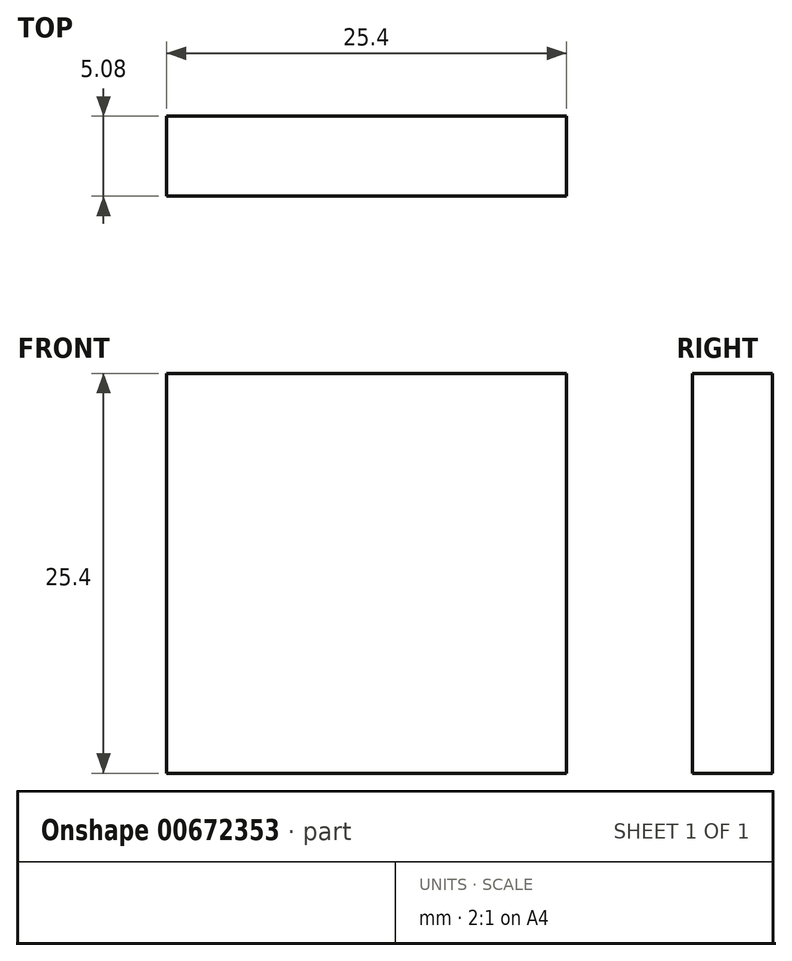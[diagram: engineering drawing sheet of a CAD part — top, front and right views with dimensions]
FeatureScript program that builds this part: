
annotation { "Feature Type Name" : "Feature", "Feature Type Description" : "" }
export const myFeature = defineFeature(function(context is Context, id is Id, definition is map)
    precondition{}
    {
        {
            var Q0;
            Q0=qCreatedBy(makeId("Front.planeOp"),FACE);
            var sketch = newSketch(context, id + "F0", { "sketchPlane" : qUnion([Q0])});
            skLineSegment(sketch, "E0.bottom", {"start": v(12.7, -12.7) * mm, "end": v(-12.7, -12.7) * mm});
            skLineSegment(sketch, "E0.top", {"start": v(12.7, 12.7) * mm, "end": v(-12.7, 12.7) * mm});
            skLineSegment(sketch, "E0.left", {"start": v(12.7, -12.7) * mm, "end": v(12.7, 12.7) * mm});
            skLineSegment(sketch, "E0.right", {"start": v(-12.7, -12.7) * mm, "end": v(-12.7, 12.7) * mm});
            skPoint(sketch, "E0.middle", {"position": v(0, 0) * mm});
            skSolve(sketch);
        }
        {
            var Q0;
            Q0 = qSketchRegion(id + "F0", true);
            extrude(context, id + "F1", {"entities" : qUnion([Q0]), "oppositeDirection" : true, "depth" : 5.08 * mm, "offsetDistance" : 25.4 * mm});
        }
    });
